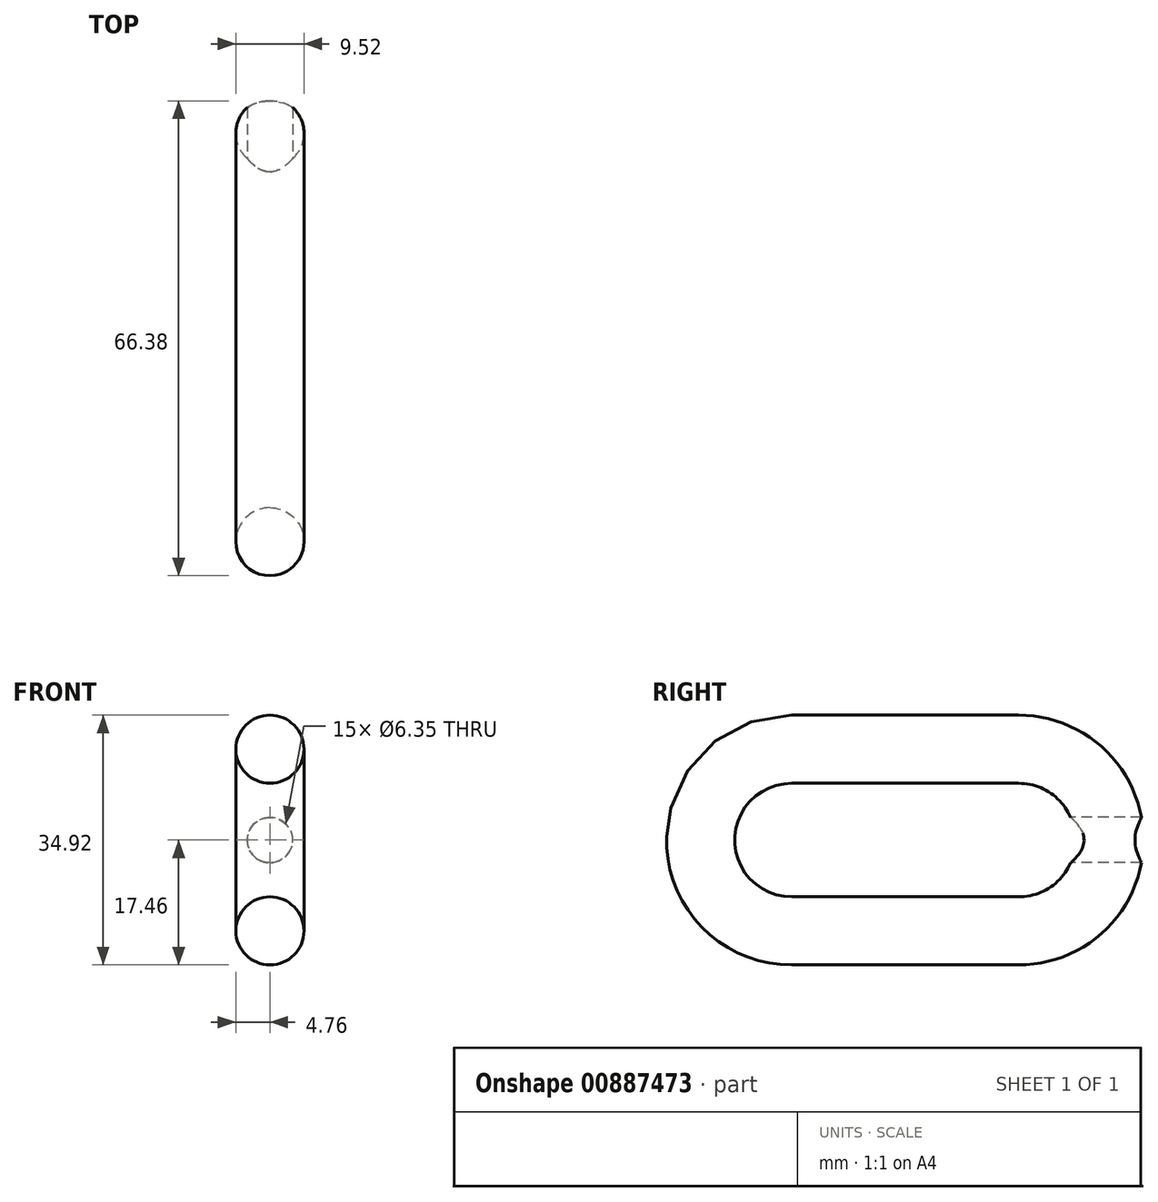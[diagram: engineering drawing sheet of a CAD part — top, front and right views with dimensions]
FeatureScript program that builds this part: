
annotation { "Feature Type Name" : "Feature", "Feature Type Description" : "" }
export const myFeature = defineFeature(function(context is Context, id is Id, definition is map)
    precondition{}
    {
        {
            var Q0;
            Q0=qCreatedBy(makeId("Front.planeOp"),FACE);
            var sketch = newSketch(context, id + "F0", { "sketchPlane" : qUnion([Q0])});
            skCircle(sketch, "E0", {"center": v(0, 0) * mm, "radius": 4.76 * mm});
            skSolve(sketch);
        }
        {
            var Q0;
            Q0=qCreatedBy(makeId("Right.planeOp"),FACE);
            var sketch = newSketch(context, id + "F1", { "sketchPlane" : qUnion([Q0])});
            skLineSegment(sketch, "E1", {"start": v(0, 0) * mm, "end": v(-25.4, 0) * mm});
            skArc(sketch, "E2", {"start": v(-25.4, 0) * mm, "mid": v(-38.1, -12.7) * mm, "end": v(-25.4, -25.4) * mm});
            skLineSegment(sketch, "E3", {"start": v(-25.4, -25.4) * mm, "end": v(6.35, -25.4) * mm});
            skLineSegment(sketch, "E4", {"start": v(0, 0) * mm, "end": v(6.35, 0) * mm});
            skArc(sketch, "E5", {"start": v(6.35, -25.4) * mm, "mid": v(19.05, -12.7) * mm, "end": v(6.35, 0) * mm});
            skSolve(sketch);
        }
        {
            var Q0;
            Q0=makeQuery(id+"F0.imprint","IMPRINT",FACE,{"disambiguationData":[TD([[makeQuery(id+"F0.imprint","IMPRINT",EDGE,{"derivedFrom":sQuery(id+"F0.wireOp",EDGE,"E0")}),1.0]])]});
            var Q1;
            Q1=sQuery(id+"F1.wireOp",EDGE,"E1");
            var Q2;
            Q2=sQuery(id+"F1.wireOp",EDGE,"E2");
            var Q3;
            Q3=sQuery(id+"F1.wireOp",EDGE,"E3");
            var Q4;
            Q4=sQuery(id+"F1.wireOp",EDGE,"E5");
            var Q5;
            Q5=sQuery(id+"F1.wireOp",EDGE,"E4");
            sweep(context, id + "F2", {"profiles" : qUnion([Q0]), "path" : qUnion([Q1, Q2, Q3, Q4, Q5])});
        }
        {
            var Q0;
            Q0=qCreatedBy(makeId("Front.planeOp"),FACE);
            var sketch = newSketch(context, id + "F3", { "sketchPlane" : qUnion([Q0])});
            skCircle(sketch, "E6", {"center": v(0, -12.7) * mm, "radius": 3.18 * mm});
            skSolve(sketch);
        }
        {
            var Q0;
            Q0=makeQuery(id+"F3.imprint","IMPRINT",FACE,{"disambiguationData":[TD([[makeQuery(id+"F3.imprint","IMPRINT",EDGE,{"derivedFrom":sQuery(id+"F3.wireOp",EDGE,"E6")}),1.0]])]});
            extrude(context, id + "F4", {"entities" : qUnion([Q0]), "operationType" : NewBodyOperationType.REMOVE, "oppositeDirection" : true, "depth" : 50.8 * mm, "offsetDistance" : 25.4 * mm});
        }
    });
